# Revit family: EKF500E3 BIM position 2
name_source: partatom
category: Mechanical Equipment
revit_build: Autodesk Revit MEP 2013 (Build: 20120221_2030(x64)
units: mm (PartAtom-declared; Revit-internal decimal feet)

## types (1)
- EKF500E3
    AC Frequency Input = 50 Hz
    AC Voltage Input = 380-415V AC Three Phase
    Category = Lo-Carbon Kitchen Box Fan
    Country of Manufacture = UK
    Family = In-Line Range
    Height = 850 mm
    Height (inclusing controller) = 1017 mm
    IP Rating = IP54
    Length = 850 mm
    Manufacturer - Name = Vent-Axia Ltd
    Manufacturer - Website = www.vent-axia.com
    Maximum In-Duct Temperature = 120 Degrees C
    Motor Rating = 1.71kW Max
    Operating Temperature = (-20C to +40C)
    Part Number = EKF500E3
    Product Description = Lo-Carbon Kitchen Box Fan
    Sub Type = Lo-Carbon Kitchen Box Fan
    Warranty period = Unit 2 years                                    Motor 5 years
    Weight = 130 kg
    Width = 850 mm
    Width (including handles) = 929 mm

## geometry (parser evidence)
native form markers: Sweep x1
no freeform markers — native parametric forms only
